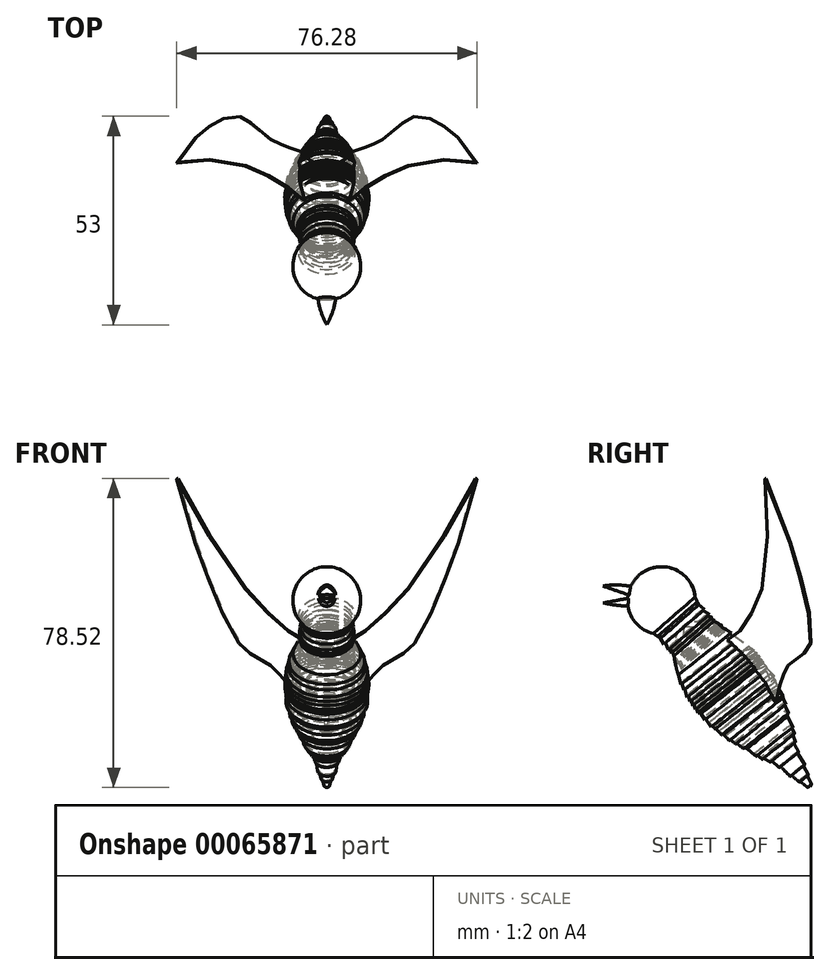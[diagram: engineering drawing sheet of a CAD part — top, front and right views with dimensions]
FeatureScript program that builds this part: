
annotation { "Feature Type Name" : "Feature", "Feature Type Description" : "" }
export const myFeature = defineFeature(function(context is Context, id is Id, definition is map)
    precondition{}
    {
        {
            var Q0;
            Q0=qCreatedBy(makeId("Right.planeOp"),FACE);
            var sketch = newSketch(context, id + "F0", { "sketchPlane" : qUnion([Q0])});
            skEllipticalArc(sketch, "E0", {});
            skLineSegment(sketch, "E1", {"start": v(-9.34, 10.8) * mm, "end": v(14.33, -19.05) * mm});
            skLineSegment(sketch, "E2", {"start": v(16.69, -10.46) * mm, "end": v(17.17, -12.04) * mm});
            skLineSegment(sketch, "E3", {"start": v(18.55, -18.42) * mm, "end": v(19.97, -21.1) * mm});
            skLineSegment(sketch, "E4", {"start": v(22, -26.74) * mm, "end": v(23.23, -29.2) * mm});
            skLineSegment(sketch, "E5", {"start": v(14.33, -19.05) * mm, "end": v(22.82, -29.75) * mm});
            skLineSegment(sketch, "E6", {"start": v(10.45, 2.2) * mm, "end": v(-5.47, -10.43) * mm, "construction": true});
            skLineSegment(sketch, "E7", {"start": v(23.23, -29.2) * mm, "end": v(22.82, -29.75) * mm});
            skLineSegment(sketch, "E8", {"start": v(18.55, -18.42) * mm, "end": v(19.14, -18.59) * mm});
            skLineSegment(sketch, "E9", {"start": v(19.97, -21.1) * mm, "end": v(19.5, -21.1) * mm});
            skLineSegment(sketch, "E10", {"start": v(19.5, -21.1) * mm, "end": v(21.52, -24.32) * mm});
            skLineSegment(sketch, "E11", {"start": v(21.52, -24.32) * mm, "end": v(21.06, -24.32) * mm});
            skLineSegment(sketch, "E12", {"start": v(21.06, -24.32) * mm, "end": v(22.45, -26.94) * mm});
            skLineSegment(sketch, "E13", {"start": v(22.45, -26.94) * mm, "end": v(22, -26.74) * mm});
            skLineSegment(sketch, "E14", {"start": v(10.45, 2.2) * mm, "end": v(11.38, 1.57) * mm});
            skLineSegment(sketch, "E15", {"start": v(11.38, 1.57) * mm, "end": v(10.94, 1.57) * mm});
            skLineSegment(sketch, "E16", {"start": v(10.94, 1.57) * mm, "end": v(12.45, 0) * mm});
            skLineSegment(sketch, "E17", {"start": v(12.45, 0) * mm, "end": v(11.82, 0.36) * mm});
            skLineSegment(sketch, "E18", {"start": v(11.82, 0.36) * mm, "end": v(13.91, -1.82) * mm});
            skLineSegment(sketch, "E19", {"start": v(13.91, -1.82) * mm, "end": v(12.78, -1.11) * mm});
            skLineSegment(sketch, "E20", {"start": v(12.8, -1.1) * mm, "end": v(14.2, -3.03) * mm});
            skLineSegment(sketch, "E21", {"start": v(14.2, -3.03) * mm, "end": v(13.64, -2.58) * mm});
            skLineSegment(sketch, "E22", {"start": v(13.64, -2.58) * mm, "end": v(15.25, -4.95) * mm});
            skLineSegment(sketch, "E23", {"start": v(15.25, -4.95) * mm, "end": v(14.43, -4.1) * mm});
            skLineSegment(sketch, "E24", {"start": v(15.04, -5.45) * mm, "end": v(16.22, -7.12) * mm});
            skLineSegment(sketch, "E25", {"start": v(16.22, -7.12) * mm, "end": v(15.25, -5.97) * mm});
            skLineSegment(sketch, "E26", {"start": v(15.25, -5.97) * mm, "end": v(16.69, -8.97) * mm});
            skLineSegment(sketch, "E27", {"start": v(16.69, -8.97) * mm, "end": v(16.12, -8.57) * mm});
            skLineSegment(sketch, "E28", {"start": v(16.12, -8.57) * mm, "end": v(17.41, -11.18) * mm});
            skLineSegment(sketch, "E29", {"start": v(17.41, -11.18) * mm, "end": v(16.69, -10.46) * mm});
            skLineSegment(sketch, "E30", {"start": v(2.87, 9.21) * mm, "end": v(5.15, 8.02) * mm});
            skLineSegment(sketch, "E31", {"start": v(5.15, 8.02) * mm, "end": v(4.57, 8.02) * mm});
            skLineSegment(sketch, "E32", {"start": v(4.57, 8.02) * mm, "end": v(6.32, 6.96) * mm});
            skLineSegment(sketch, "E33", {"start": v(6.32, 6.96) * mm, "end": v(5.88, 6.96) * mm});
            skLineSegment(sketch, "E34", {"start": v(5.88, 6.96) * mm, "end": v(7.9, 5.76) * mm});
            skLineSegment(sketch, "E35", {"start": v(7.9, 5.76) * mm, "end": v(7.2, 5.76) * mm});
            skLineSegment(sketch, "E36", {"start": v(7.2, 5.76) * mm, "end": v(8.83, 4.78) * mm});
            skLineSegment(sketch, "E37", {"start": v(8.83, 4.78) * mm, "end": v(8.2, 4.78) * mm});
            skLineSegment(sketch, "E38", {"start": v(8.2, 4.78) * mm, "end": v(9.68, 3.88) * mm});
            skLineSegment(sketch, "E39", {"start": v(9.68, 3.88) * mm, "end": v(9.03, 3.88) * mm});
            skLineSegment(sketch, "E40", {"start": v(9.03, 3.88) * mm, "end": v(10.46, 3.01) * mm});
            skLineSegment(sketch, "E41", {"start": v(10.46, 3.01) * mm, "end": v(9.78, 3.01) * mm});
            skLineSegment(sketch, "E42", {"start": v(9.78, 3.01) * mm, "end": v(11.1, 2.21) * mm});
            skLineSegment(sketch, "E43", {"start": v(11.1, 2.21) * mm, "end": v(10.45, 2.2) * mm});
            skEllipticalArc(sketch, "E44.trimOffspring", {});
            skLineSegment(sketch, "E45", {"start": v(16.69, -10.46) * mm, "end": v(16.5, -10.27) * mm});
            skLineSegment(sketch, "E46", {"start": v(17.17, -12.04) * mm, "end": v(18.55, -14.82) * mm});
            skLineSegment(sketch, "E47", {"start": v(18.55, -14.82) * mm, "end": v(17.8, -14.17) * mm});
            skLineSegment(sketch, "E48", {"start": v(17.81, -14.17) * mm, "end": v(18.95, -16.5) * mm});
            skLineSegment(sketch, "E49", {"start": v(18.95, -16.5) * mm, "end": v(18.35, -15.97) * mm});
            skLineSegment(sketch, "E50.trimOffspring", {"start": v(18.35, -15.97) * mm, "end": v(19.14, -18.59) * mm});
            const initialGuessF0  = {"E0": [0.0024933195672929304, -0.004120009485632183, 0.6212981181772816, -0.7835742774934413, 0.01905, 0.01016, 2.136688247193005, 0], "E44.trimOffspring": [0.0024933195672929304, -0.004120009485632183, 0.6212981181772816, -0.7835742774934413, 0.01905, 0.01016, 1.0885486790265921, 1.1717906865129262]};
            skSetInitialGuess(sketch, initialGuessF0);
            skSolve(sketch);
        }
        {
            var Q0;
            {var subQ0=sQuery(id+"F0.wireOp",EDGE,"E1");Q0=makeQuery(id+"F0.imprint","IMPRINT",FACE,{"disambiguationData":[TD([[makeQuery(id+"F0.imprint","IMPRINT",EDGE,{"derivedFrom":subQ0}),1.0]])]});}
            var Q1;
            {var subQ0=sQuery(id+"F0.wireOp",EDGE,"KMg9PYZW-iAyn-2mjM-nuoA-7G5tMEvxgTKv");Q1=makeQuery(id+"F0.imprint","IMPRINT",FACE,{"disambiguationData":[TD([[makeQuery(id+"F0.imprint","IMPRINT",EDGE,{"derivedFrom":subQ0}),-1.0]])]});}
            var Q2;
            {var subQ0=sQuery(id+"F0.wireOp",EDGE,"E3");Q2=makeQuery(id+"F0.imprint","IMPRINT",FACE,{"disambiguationData":[TD([[makeQuery(id+"F0.imprint","IMPRINT",EDGE,{"derivedFrom":subQ0}),-1.0]])]});}
            var Q3;
            Q3=sQuery(id+"F0.wireOp",EDGE,"E1");
            revolve(context, id + "F1", {"entities" : qUnion([Q0, Q1, Q2]), "axis" : qUnion([Q3]), "revolveType" : RevolveType.FULL});
        }
        {
            var Q0;
            Q0=qCreatedBy(makeId("Right.planeOp"),FACE);
            var sketch = newSketch(context, id + "F2", { "sketchPlane" : qUnion([Q0])});
            skCircle(sketch, "E51", {"center": v(-14.9, 17.4) * mm, "radius": 8.62 * mm});
            skLineSegment(sketch, "E52", {"start": v(-9.23, 10.9) * mm, "end": v(-20.56, 23.9) * mm});
            skLineSegment(sketch, "E53", {"start": v(-0.26, 11.1) * mm, "end": v(0, 10.9) * mm});
            skLineSegment(sketch, "E54", {"start": v(-9.23, 10.9) * mm, "end": v(0.91, 10.13) * mm});
            skLineSegment(sketch, "E55", {"start": v(0, 10.9) * mm, "end": v(0.85, 10.48) * mm});
            skLineSegment(sketch, "E56", {"start": v(0.85, 10.48) * mm, "end": v(0.54, 10.48) * mm});
            skLineSegment(sketch, "E57", {"start": v(0.54, 10.48) * mm, "end": v(1.66, 10.1) * mm});
            skLineSegment(sketch, "E58", {"start": v(1.66, 10.1) * mm, "end": v(0.91, 10.13) * mm});
            skLineSegment(sketch, "E59", {"start": v(-3.67, 13.7) * mm, "end": v(-2, 13.1) * mm});
            skLineSegment(sketch, "E60", {"start": v(-2, 13.1) * mm, "end": v(-2.9, 13.1) * mm});
            skLineSegment(sketch, "E61", {"start": v(-2.9, 13.1) * mm, "end": v(-1.36, 12.36) * mm});
            skLineSegment(sketch, "E62", {"start": v(-1.36, 12.36) * mm, "end": v(-1.92, 12.36) * mm});
            skLineSegment(sketch, "E63", {"start": v(-1.92, 12.36) * mm, "end": v(-0.37, 11.6) * mm});
            skLineSegment(sketch, "E64", {"start": v(-0.37, 11.6) * mm, "end": v(-0.93, 11.6) * mm});
            skLineSegment(sketch, "E65", {"start": v(-0.93, 11.6) * mm, "end": v(0.54, 11.1) * mm});
            skLineSegment(sketch, "E66", {"start": v(0.54, 11.1) * mm, "end": v(-0.26, 11.1) * mm});
            skLineSegment(sketch, "E67", {"start": v(-6.33, 18.33) * mm, "end": v(-5.8, 17.11) * mm});
            skLineSegment(sketch, "E68", {"start": v(-5.8, 17.11) * mm, "end": v(-5.39, 16.37) * mm});
            skLineSegment(sketch, "E69", {"start": v(-5.39, 16.37) * mm, "end": v(-4.03, 15.21) * mm});
            skLineSegment(sketch, "E70", {"start": v(-4.03, 15.21) * mm, "end": v(-4.6, 15.04) * mm});
            skLineSegment(sketch, "E71", {"start": v(-4.6, 15.04) * mm, "end": v(-2.71, 13.94) * mm});
            skLineSegment(sketch, "E72", {"start": v(-2.71, 13.94) * mm, "end": v(-3.67, 13.7) * mm});
            skSolve(sketch);
        }
        {
            var Q0;
            {var subQ0=sQuery(id+"F2.wireOp",EDGE,"E52");Q0=makeQuery(id+"F2.imprint","IMPRINT",FACE,{"disambiguationData":[TD([[makeQuery(id+"F2.imprint","IMPRINT",EDGE,{"derivedFrom":subQ0}),-1.0]])]});}
            var Q1;
            {var subQ0=sQuery(id+"F2.wireOp",EDGE,"rIAOiIP5-GcvB-seYg-YOrj-JQtnw5JkNV3g");Q1=makeQuery(id+"F2.imprint","IMPRINT",FACE,{"disambiguationData":[TD([[makeQuery(id+"F2.imprint","IMPRINT",EDGE,{"derivedFrom":subQ0}),-1.0]])]});}
            var Q2;
            Q2=makeQuery(id+"F2.imprint","IMPRINT",FACE,{"disambiguationData":[TD([[makeQuery(id+"F2.imprint","IMPRINT",EDGE,{"derivedFrom":sQuery(id+"F2.wireOp",EDGE,"E53")}),-1.0]])]});
            var Q3;
            Q3=sQuery(id+"F2.wireOp",EDGE,"E52");
            revolve(context, id + "F3", {"entities" : qUnion([Q0, Q1, Q2]), "axis" : qUnion([Q3]), "revolveType" : RevolveType.FULL});
        }
        {
            var Q0;
            Q0=qCreatedBy(makeId("Right.planeOp"),FACE);
            var sketch = newSketch(context, id + "F4", { "sketchPlane" : qUnion([Q0])});
            skLineSegment(sketch, "E73", {"start": v(-29.77, 21.1) * mm, "end": v(-22.55, 18.63) * mm});
            skLineSegment(sketch, "E74", {"start": v(-22.55, 18.63) * mm, "end": v(-21.85, 20.83) * mm});
            skArc(sketch, "E75", {"start": v(-21.85, 20.83) * mm, "mid": v(-25.8, 21.37) * mm, "end": v(-29.77, 21.1) * mm});
            skLineSegment(sketch, "E76", {"start": v(-29.7, 16.83) * mm, "end": v(-21.96, 18.25) * mm});
            skLineSegment(sketch, "E77", {"start": v(-21.96, 18.25) * mm, "end": v(-22.19, 15.95) * mm});
            skArc(sketch, "E78", {"start": v(-29.7, 16.83) * mm, "mid": v(-25.97, 16.2) * mm, "end": v(-22.19, 15.95) * mm});
            skSolve(sketch);
        }
        {
            var Q0;
            Q0=makeQuery(id+"F4.imprint","IMPRINT",FACE,{"disambiguationData":[TD([[makeQuery(id+"F4.imprint","IMPRINT",EDGE,{"derivedFrom":sQuery(id+"F4.wireOp",EDGE,"E73")}),1.0]])]});
            var Q1;
            Q1=sQuery(id+"F4.wireOp",EDGE,"E73");
            revolve(context, id + "F5", {"operationType" : NewBodyOperationType.ADD, "entities" : qUnion([Q0]), "axis" : qUnion([Q1]), "revolveType" : RevolveType.SYMMETRIC, "angle" : 180 * degree});
        }
        {
            var Q0;
            Q0=makeQuery(id+"F4.imprint","IMPRINT",FACE,{"disambiguationData":[TD([[makeQuery(id+"F4.imprint","IMPRINT",EDGE,{"derivedFrom":sQuery(id+"F4.wireOp",EDGE,"E76")}),-1.0]])]});
            var Q1;
            Q1=sQuery(id+"F4.wireOp",EDGE,"E76");
            revolve(context, id + "F6", {"operationType" : NewBodyOperationType.ADD, "entities" : qUnion([Q0]), "axis" : qUnion([Q1]), "revolveType" : RevolveType.SYMMETRIC, "angle" : 180 * degree});
        }
        {
            var Q0;
            Q0=qCreatedBy(makeId("Right.planeOp"),FACE);
            var sketch = newSketch(context, id + "F7", { "sketchPlane" : qUnion([Q0])});
            skLineSegment(sketch, "E79", {"start": v(-18.79, 24.93) * mm, "end": v(18.79, -24.93) * mm, "construction": true});
            skLineSegment(sketch, "E80", {"start": v(3.57, 8.6) * mm, "end": v(8.25, 12.13) * mm});
            skLineSegment(sketch, "E81", {"start": v(8.25, 12.13) * mm, "end": v(12.97, 17.94) * mm});
            skLineSegment(sketch, "E82", {"start": v(12.97, 17.94) * mm, "end": v(17.46, 25.6) * mm});
            skLineSegment(sketch, "E83", {"start": v(17.46, 25.6) * mm, "end": v(21.92, 41.21) * mm});
            skLineSegment(sketch, "E84", {"start": v(28.76, 40.39) * mm, "end": v(30.32, 30.69) * mm});
            skLineSegment(sketch, "E85", {"start": v(30.32, 30.69) * mm, "end": v(31.2, 20.76) * mm});
            skLineSegment(sketch, "E86", {"start": v(31.2, 20.76) * mm, "end": v(30.32, 12.13) * mm});
            skLineSegment(sketch, "E87", {"start": v(30.32, 12.13) * mm, "end": v(27.75, 8.86) * mm});
            skLineSegment(sketch, "E88", {"start": v(27.75, 8.86) * mm, "end": v(21.92, 4.47) * mm});
            skLineSegment(sketch, "E89", {"start": v(21.92, 41.21) * mm, "end": v(23.97, 57.8) * mm});
            skLineSegment(sketch, "E90", {"start": v(23.97, 57.8) * mm, "end": v(28.76, 40.39) * mm});
            skLineSegment(sketch, "E91", {"start": v(3.57, 8.6) * mm, "end": v(8.7, 4.76) * mm});
            skLineSegment(sketch, "E92", {"start": v(8.7, 4.76) * mm, "end": v(10.6, 2.38) * mm});
            skLineSegment(sketch, "E93", {"start": v(10.6, 2.38) * mm, "end": v(12.2, 0) * mm});
            skLineSegment(sketch, "E94", {"start": v(12.2, 0) * mm, "end": v(13.78, -1.6) * mm});
            skLineSegment(sketch, "E95", {"start": v(13.78, -1.6) * mm, "end": v(16.1, -7.1) * mm});
            skLineSegment(sketch, "E96", {"start": v(16.1, -7.1) * mm, "end": v(18.4, -1.6) * mm});
            skLineSegment(sketch, "E97", {"start": v(18.4, -1.6) * mm, "end": v(19.98, 1.5) * mm});
            skLineSegment(sketch, "E98", {"start": v(19.98, 1.5) * mm, "end": v(21.92, 4.47) * mm});
            skSolve(sketch);
        }
        {
            var Q0;
            Q0=makeQuery(id+"F7.imprint","IMPRINT",FACE,{"disambiguationData":[TD([[makeQuery(id+"F7.imprint","IMPRINT",EDGE,{"derivedFrom":sQuery(id+"F7.wireOp",EDGE,"RfXKZFLl-hwVC-KUTW-NXVo-ru393bOjjmmP")}),-1.0]])]});
            var Q1;
            Q1=makeQuery(id+"F7.imprint","IMPRINT",FACE,{"disambiguationData":[TD([[makeQuery(id+"F7.imprint","IMPRINT",EDGE,{"derivedFrom":sQuery(id+"F7.wireOp",EDGE,"E80")}),-1.0]])]});
            var Q2;
            Q2=sQuery(id+"F7.wireOp",EDGE,"E79");
            revolve(context, id + "F8", {"operationType" : NewBodyOperationType.ADD, "entities" : qUnion([Q0, Q1]), "axis" : qUnion([Q2]), "revolveType" : RevolveType.SYMMETRIC, "angle" : 90 * degree});
        }
        {
            var Q0;
            Q0 = qSketchRegion(id + "F7", true);
            var Q1;
            Q1=sQuery(id+"F7.wireOp",EDGE,"E79");
            revolve(context, id + "F9", {"operationType" : NewBodyOperationType.REMOVE, "entities" : qUnion([Q0]), "axis" : qUnion([Q1]), "revolveType" : RevolveType.SYMMETRIC, "angle" : 89 * degree});
        }
        {
            var Q0;
            Q0=makeQuery(id+"F1.opRevolve","SWEPT_EDGE",EDGE,{"disambiguationData":[OSD([sQuery(id+"F0.wireOp",EDGE,"E46"),sQuery(id+"F0.wireOp",EDGE,"E47")])]});
            var Q1;
            Q1=makeQuery(id+"F1.opRevolve","SWEPT_EDGE",EDGE,{"disambiguationData":[OSD([sQuery(id+"F0.wireOp",EDGE,"E49"),sQuery(id+"F0.wireOp",EDGE,"E50.trimOffspring")])]});
            var Q2;
            Q2=makeQuery(id+"F1.opRevolve","SWEPT_EDGE",EDGE,{"disambiguationData":[OSD([sQuery(id+"F0.wireOp",EDGE,"E3"),sQuery(id+"F0.wireOp",EDGE,"E8")])]});
            var Q3;
            Q3=makeQuery(id+"F1.opRevolve","SWEPT_EDGE",EDGE,{"disambiguationData":[OSD([sQuery(id+"F0.wireOp",EDGE,"E4"),sQuery(id+"F0.wireOp",EDGE,"E7")])]});
            var Q4;
            Q4=makeQuery(id+"F1.opRevolve","SWEPT_EDGE",EDGE,{"disambiguationData":[OSD([sQuery(id+"F0.wireOp",EDGE,"E9"),sQuery(id+"F0.wireOp",EDGE,"E10")])]});
            var Q5;
            Q5=makeQuery(id+"F1.opRevolve","SWEPT_EDGE",EDGE,{"disambiguationData":[OSD([sQuery(id+"F0.wireOp",EDGE,"E11"),sQuery(id+"F0.wireOp",EDGE,"E12")])]});
            var Q6;
            Q6=makeQuery(id+"F1.opRevolve","SWEPT_EDGE",EDGE,{"disambiguationData":[OSD([sQuery(id+"F0.wireOp",EDGE,"E4"),sQuery(id+"F0.wireOp",EDGE,"E13")])]});
            var Q7;
            Q7=makeQuery(id+"F1.opRevolve","SWEPT_EDGE",EDGE,{"disambiguationData":[OSD([sQuery(id+"F0.wireOp",EDGE,"E3"),sQuery(id+"F0.wireOp",EDGE,"E9")])]});
            var Q8;
            Q8=makeQuery(id+"F1.opRevolve","SWEPT_EDGE",EDGE,{"disambiguationData":[OSD([sQuery(id+"F0.wireOp",EDGE,"E8"),sQuery(id+"F0.wireOp",EDGE,"E50.trimOffspring")])]});
            var Q9;
            Q9=makeQuery(id+"F1.opRevolve","SWEPT_EDGE",EDGE,{"disambiguationData":[OSD([sQuery(id+"F0.wireOp",EDGE,"E48"),sQuery(id+"F0.wireOp",EDGE,"E49")])]});
            var Q10;
            Q10=makeQuery(id+"F1.opRevolve","SWEPT_EDGE",EDGE,{"disambiguationData":[OSD([sQuery(id+"F0.wireOp",EDGE,"E10"),sQuery(id+"F0.wireOp",EDGE,"E11")])]});
            var Q11;
            Q11=makeQuery(id+"F1.opRevolve","SWEPT_EDGE",EDGE,{"disambiguationData":[OSD([sQuery(id+"F0.wireOp",EDGE,"E12"),sQuery(id+"F0.wireOp",EDGE,"E13")])]});
            fillet(context, id + "F10", {"entities" : qUnion([Q0, Q1, Q2, Q3, Q4, Q5, Q6, Q7, Q8, Q9, Q10, Q11]), "radius" : 0.03 * mm, "tangentPropagation" : true, "allowEdgeOverflow" : false});
        }
    });
